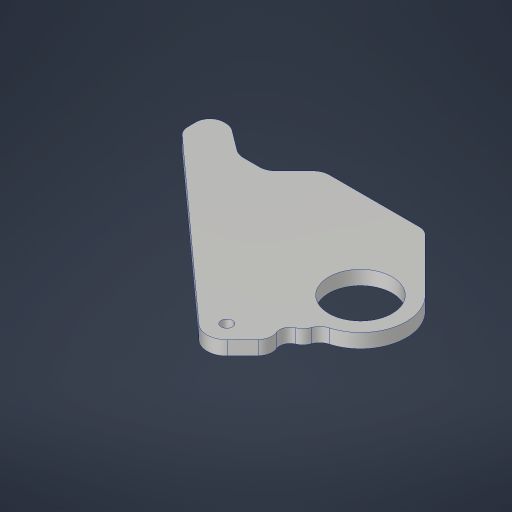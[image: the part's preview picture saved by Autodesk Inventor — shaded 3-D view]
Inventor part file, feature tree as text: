
AUTODESK INVENTOR PART (.ipt)
format: ipt  version: 2023.4 (Build 274418000, 418)  size: 229,888 bytes
history: native  units: in
note: dims shown in document units (in); Inventor stores cm internally (conversion verified against a paired STEP export)
features: fillet x2, sketch x1, extrude x1, hole x1
ambient origin geometry x8: Origin, YZ Plane, XZ Plane, XY Plane, X Axis, Y Axis, Z Axis, Center Point
bodies: Solid1 (feature_tree)
feature tree (5):
  sketch  "Sketch1"  dims[d0=1.315in d1=1.125in d2=0.25in d3=0.375in d4=1.25in d5=0.201in d6=0.25in d7=0.75in d8=0.375in d9=1.0in d10=1.0in d11=0.5in d12=0.5in d13=0.5in d15=3.0in d16=3.0in d17=0.5in d18=0.125in d19=0.375in d20=0.5in d23=0.25in d24=0.0in d25=0.25in d26=0.3in d27=0.201in d28=0.75in d29=0.385in d30=0.25in d31=0.5635in d32=1.0in d33=0.8108in d34=0.175in d35=0.05in d36=0.05in]
  extrude  "Extrusion1"  Depth=0.25in
  fillet  "Fillet1"  Radius=0.25in
  fillet  "Fillet2"  Radius=0.375in
  hole  "Hole1"  [1 undecoded]
note: 1 required parameter value undecoded (feature->parameter linkage not recoverable at this tier; creation-order binding heuristic only, values carry confidence <= 0.55)
